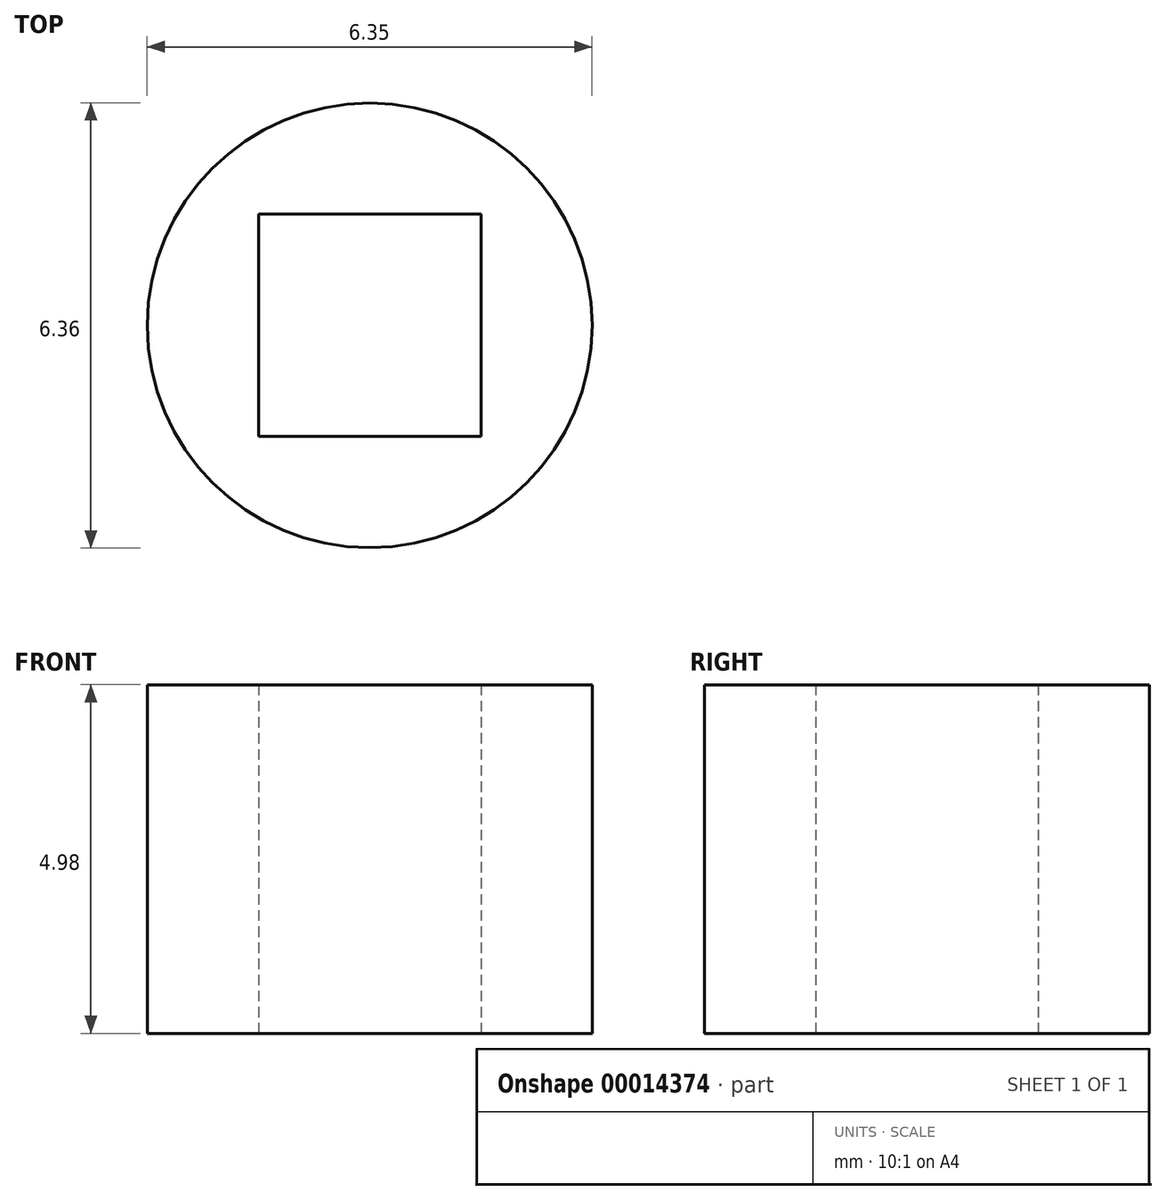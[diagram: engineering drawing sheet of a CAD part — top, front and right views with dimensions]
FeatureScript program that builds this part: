
annotation { "Feature Type Name" : "Feature", "Feature Type Description" : "" }
export const myFeature = defineFeature(function(context is Context, id is Id, definition is map)
    precondition{}
    {
        {
            var Q0;
            Q0=qCreatedBy(makeId("Top.planeOp"),FACE);
            var sketch = newSketch(context, id + "F0", { "sketchPlane" : qUnion([Q0])});
            skCircle(sketch, "E0", {"center": v(-1.07, 0) * mm, "radius": 3.18 * mm});
            skLineSegment(sketch, "E1.rect.bottom", {"start": v(-2.66, 1.59) * mm, "end": v(0.51, 1.59) * mm});
            skLineSegment(sketch, "E1.rect.top", {"start": v(-2.66, -1.59) * mm, "end": v(0.51, -1.59) * mm});
            skLineSegment(sketch, "E1.rect.left", {"start": v(-2.66, 1.59) * mm, "end": v(-2.66, -1.59) * mm});
            skLineSegment(sketch, "E1.rect.right", {"start": v(0.51, 1.59) * mm, "end": v(0.51, -1.59) * mm});
            skSolve(sketch);
        }
        {
            var Q0;
            Q0=qSketchRegion(id+"F0",true);
            extrude(context, id + "F1", {"entities" : qUnion([Q0]), "depth" : 4.98 * mm});
        }
    });
